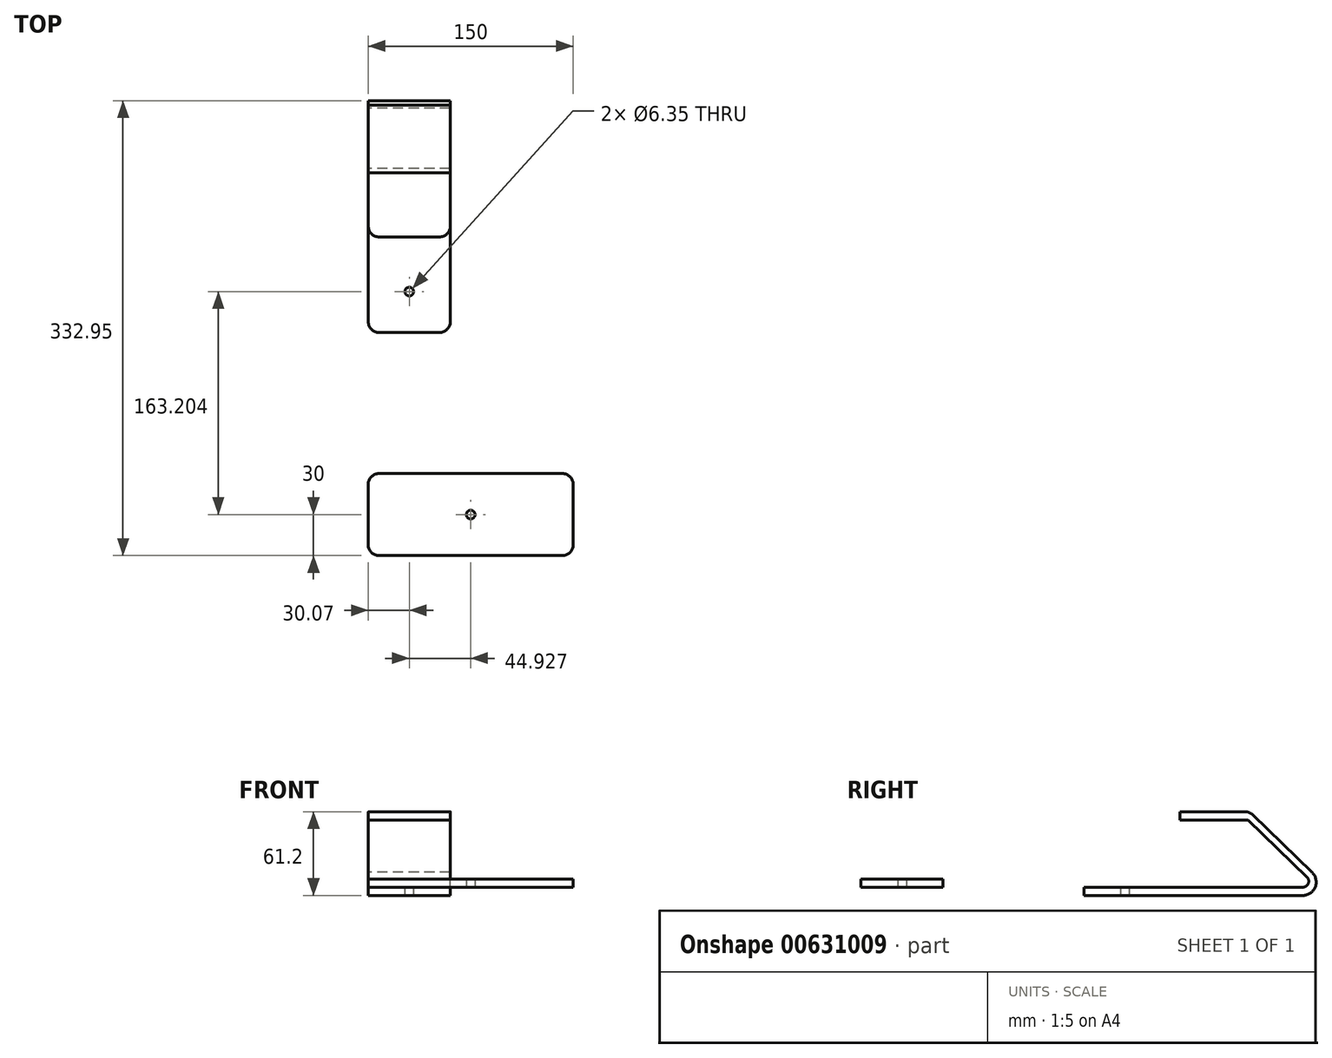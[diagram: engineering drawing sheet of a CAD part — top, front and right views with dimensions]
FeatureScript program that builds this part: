
annotation { "Feature Type Name" : "Feature", "Feature Type Description" : "" }
export const myFeature = defineFeature(function(context is Context, id is Id, definition is map)
    precondition{}
    {
        {
            var Q0;
            Q0=qCreatedBy(makeId("Top.planeOp"),FACE);
            var sketch = newSketch(context, id + "F0", { "sketchPlane" : qUnion([Q0])});
            skLineSegment(sketch, "E0.bottom", {"start": v(7.93, 60) * mm, "end": v(141.93, 60) * mm});
            skLineSegment(sketch, "E0.top", {"start": v(7.93, 0) * mm, "end": v(141.93, 0) * mm});
            skLineSegment(sketch, "E0.left", {"start": v(-0.07, 52) * mm, "end": v(-0.07, 8) * mm});
            skLineSegment(sketch, "E0.right", {"start": v(149.93, 52) * mm, "end": v(149.93, 8) * mm});
            skPoint(sketch, "E1.visualSharp", {"position": v(149.93, 60) * mm});
            skArc(sketch, "E1.filletArc", {"start": v(149.93, 52) * mm, "mid": v(147.58, 57.66) * mm, "end": v(141.93, 60) * mm});
            skPoint(sketch, "E2.visualSharp", {"position": v(149.93, 0) * mm});
            skArc(sketch, "E2.filletArc", {"start": v(141.93, 0) * mm, "mid": v(147.58, 2.34) * mm, "end": v(149.93, 8) * mm});
            skPoint(sketch, "E3.visualSharp", {"position": v(-0.07, 0) * mm});
            skArc(sketch, "E3.filletArc", {"start": v(-0.07, 8) * mm, "mid": v(2.27, 2.34) * mm, "end": v(7.93, 0) * mm});
            skPoint(sketch, "E4.visualSharp", {"position": v(-0.07, 60) * mm});
            skArc(sketch, "E4.filletArc", {"start": v(7.93, 60) * mm, "mid": v(2.27, 57.66) * mm, "end": v(-0.07, 52) * mm});
            skSolve(sketch);
        }
        {
            var Q0;
            Q0=makeQuery(id+"F0.imprint","IMPRINT",FACE,{"disambiguationData":[TD([[makeQuery(id+"F0.imprint","IMPRINT",EDGE,{"derivedFrom":sQuery(id+"F0.wireOp",EDGE,"E0.bottom")}),-1.0]])]});
            var sketch = newSketch(context, id + "F1", { "sketchPlane" : qUnion([Q0])});
            skPoint(sketch, "E5", {"position": v(74.93, 30) * mm});
            skCircle(sketch, "E6", {"center": v(74.93, 30) * mm, "radius": 3.18 * mm});
            skSolve(sketch);
        }
        {
            var Q0;
            Q0 = qSketchRegion(id + "F0", true);
            var sketch = newSketch(context, id + "F2", { "sketchPlane" : qUnion([Q0])});
            skSolve(sketch);
        }
        {
            var Q0;
            Q0 = qSketchRegion(id + "F2", true);
            var Q1;
            Q1=makeQuery(id+"F1.imprint","IMPRINT",FACE,{"disambiguationData":[TD([[makeQuery(id+"F1.imprint","IMPRINT",EDGE,{"derivedFrom":sQuery(id+"F1.wireOp",EDGE,"E6")}),-1.0]])]});
            extrude(context, id + "F3", {"entities" : qUnion([Q0, Q1]), "depth" : 6 * mm, "offsetDistance" : 25 * mm});
        }
        {
            var Q0;
            Q0=qCreatedBy(makeId("Right.planeOp"),FACE);
            var sketch = newSketch(context, id + "F4", { "sketchPlane" : qUnion([Q0])});
            skLineSegment(sketch, "E7", {"start": v(163.2, -6) * mm, "end": v(323.2, -6) * mm});
            skLineSegment(sketch, "E8", {"start": v(163.2, -6) * mm, "end": v(163.2, 0) * mm});
            skLineSegment(sketch, "E9", {"start": v(163.2, 0) * mm, "end": v(323.2, 0) * mm});
            skArc(sketch, "E10", {"start": v(323.2, -6) * mm, "mid": v(332.32, 0.3) * mm, "end": v(329.66, 11.04) * mm});
            skArc(sketch, "E11", {"start": v(323.2, 0) * mm, "mid": v(327.17, 2.67) * mm, "end": v(326.19, 7.35) * mm});
            skLineSegment(sketch, "E12", {"start": v(326.19, 7.35) * mm, "end": v(283.15, 49.16) * mm});
            skLineSegment(sketch, "E13", {"start": v(329.66, 11.04) * mm, "end": v(286.62, 52.85) * mm});
            skLineSegment(sketch, "E14", {"start": v(283.15, 49.16) * mm, "end": v(233.15, 49.16) * mm});
            skLineSegment(sketch, "E15", {"start": v(233.15, 49.16) * mm, "end": v(233.15, 55.16) * mm});
            skLineSegment(sketch, "E16", {"start": v(233.15, 55.16) * mm, "end": v(277.55, 55.16) * mm});
            skArc(sketch, "E17", {"start": v(286.62, 52.85) * mm, "mid": v(283.56, 54.74) * mm, "end": v(279.99, 55.16) * mm});
            skLineSegment(sketch, "E18", {"start": v(277.55, 55.16) * mm, "end": v(279.99, 55.16) * mm});
            skSolve(sketch);
        }
        {
            var Q0;
            Q0 = qSketchRegion(id + "F4", true);
            extrude(context, id + "F5", {"entities" : qUnion([Q0]), "depth" : 60 * mm, "offsetDistance" : 25 * mm});
        }
        {
            var Q0;
            Q0=makeQuery(id+"F5.opExtrude","SWEPT_FACE",FACE,{"disambiguationData":[OSD([sQuery(id+"F4.wireOp",EDGE,"E9")])]});
            var sketch = newSketch(context, id + "F6", { "sketchPlane" : qUnion([Q0])});
            skPoint(sketch, "E19", {"position": v(30, 193.2) * mm});
            skCircle(sketch, "E20", {"center": v(30, 193.2) * mm, "radius": 3.18 * mm});
            skSolve(sketch);
        }
        {
            var Q0;
            Q0 = qSketchRegion(id + "F6", true);
            var sketch = newSketch(context, id + "F7", { "sketchPlane" : qUnion([Q0])});
            skSolve(sketch);
        }
        {
            var Q0;
            Q0 = qSketchRegion(id + "F7", true);
            var Q1;
            Q1=makeQuery(id+"F6.imprint","IMPRINT",FACE,{"disambiguationData":[TD([[makeQuery(id+"F6.imprint","IMPRINT",EDGE,{"derivedFrom":sQuery(id+"F6.wireOp",EDGE,"E20")}),1.0]])]});
            extrude(context, id + "F8", {"entities" : qUnion([Q0, Q1]), "operationType" : NewBodyOperationType.REMOVE, "oppositeDirection" : true, "depth" : 25 * mm, "offsetDistance" : 25 * mm});
        }
        {
            var Q0;
            Q0=makeQuery(id+"F5.opExtrude","CAP_FACE",FACE,{"disambiguationData":[OSD([sQuery(id+"F4.wireOp",EDGE,"E7"),sQuery(id+"F4.wireOp",EDGE,"E8"),sQuery(id+"F4.wireOp",EDGE,"E9"),sQuery(id+"F4.wireOp",EDGE,"E10"),sQuery(id+"F4.wireOp",EDGE,"E11"),sQuery(id+"F4.wireOp",EDGE,"E12"),sQuery(id+"F4.wireOp",EDGE,"E13"),sQuery(id+"F4.wireOp",EDGE,"E14"),sQuery(id+"F4.wireOp",EDGE,"E15"),sQuery(id+"F4.wireOp",EDGE,"E16"),sQuery(id+"F4.wireOp",EDGE,"E17"),sQuery(id+"F4.wireOp",EDGE,"E18")])],"isStart":false});
            var sketch = newSketch(context, id + "F9", { "sketchPlane" : qUnion([Q0])});
            skSolve(sketch);
        }
        {
            var Q0;
            Q0=makeQuery(id+"F5.opExtrude","CAP_EDGE",EDGE,{"disambiguationData":[OSD([sQuery(id+"F4.wireOp",EDGE,"E8")])],"isStart":false});
            var Q1;
            Q1=makeQuery(id+"F5.opExtrude","CAP_EDGE",EDGE,{"disambiguationData":[OSD([sQuery(id+"F4.wireOp",EDGE,"E8")])],"isStart":true});
            fillet(context, id + "F10", {"entities" : qUnion([Q0, Q1]), "radius" : 8 * mm, "tangentPropagation" : true, "allowEdgeOverflow" : false});
        }
        {
            var Q0;
            Q0=makeQuery(id+"F5.opExtrude","CAP_EDGE",EDGE,{"disambiguationData":[OSD([sQuery(id+"F4.wireOp",EDGE,"E15")])],"isStart":false});
            var Q1;
            Q1=makeQuery(id+"F5.opExtrude","CAP_EDGE",EDGE,{"disambiguationData":[OSD([sQuery(id+"F4.wireOp",EDGE,"E15")])],"isStart":true});
            fillet(context, id + "F11", {"entities" : qUnion([Q0, Q1]), "radius" : 8 * mm, "tangentPropagation" : true, "allowEdgeOverflow" : false});
        }
    });
